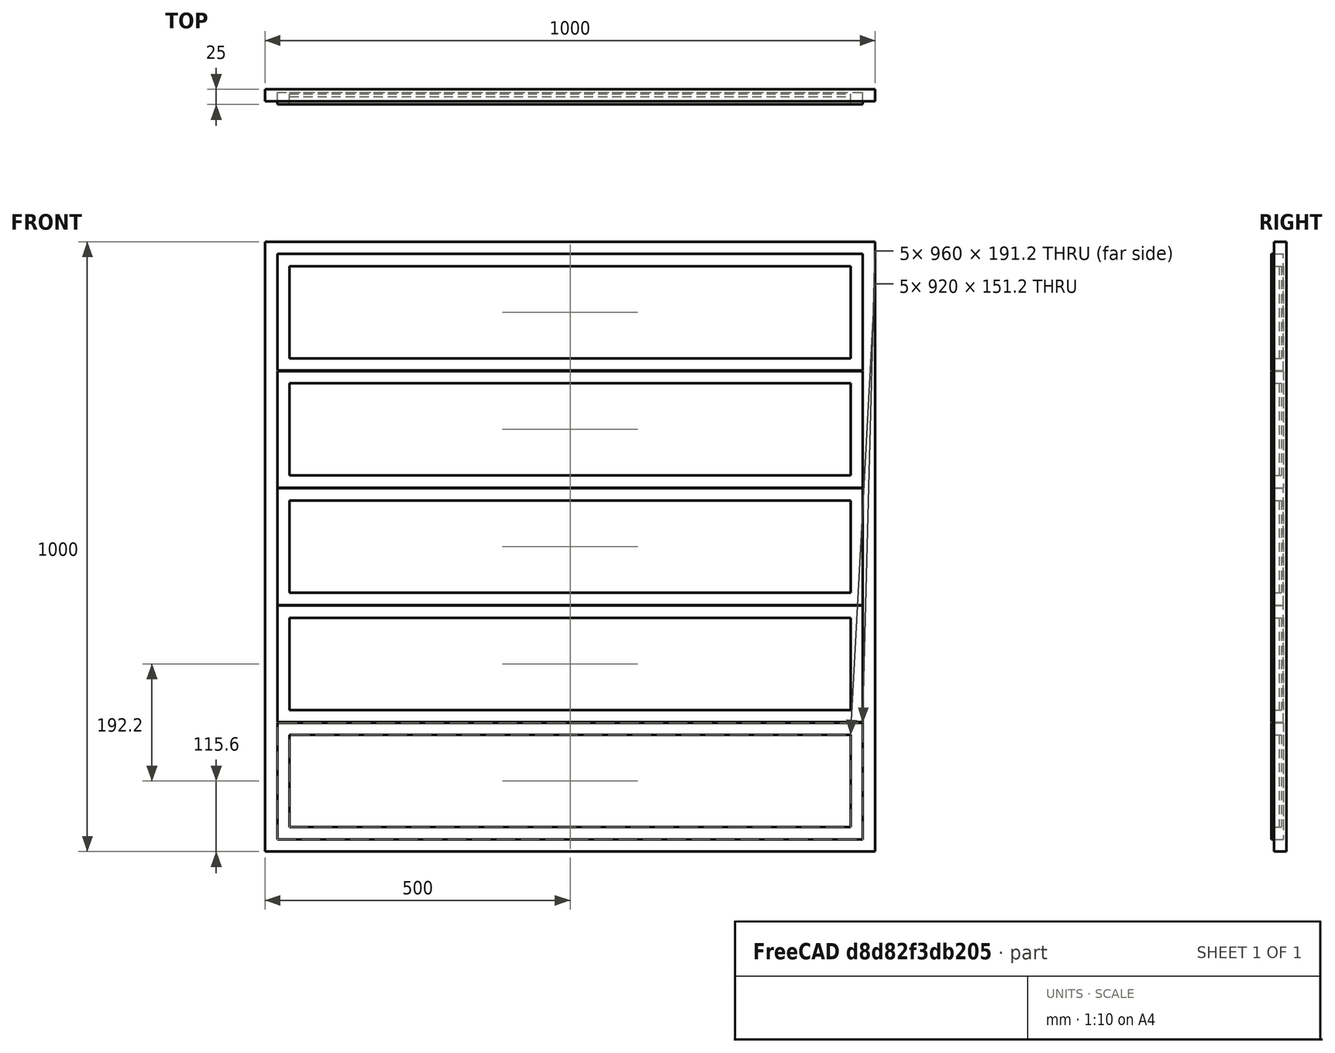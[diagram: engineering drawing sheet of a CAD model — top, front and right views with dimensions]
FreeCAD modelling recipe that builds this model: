
FCSTD DOCUMENT  (FreeCAD 0.16R6704 (Git))
Label: Tilting window 5 modules
License: CreativeCommons Attribution
LicenseURL: http://creativecommons.org/licenses/by/4.0/
objects: Sketcher::SketchObject×1, Part::FeaturePython×1
note: 2 computed .brp shape members not serialized (recipe doc carries the construction recipe); baked Part::Feature solids carry a one-line shape summary decoded from their .brp

FEATURE [Sketcher::SketchObject] Sketch107
  Placement = pos=(0,0,0) rot=(1,0,0;1.5708rad)
  sketch-geometry (54):
    g0: LineSegment StartX=0 StartY=1000 StartZ=0 EndX=1000 EndY=1000 EndZ=0
    g1: LineSegment StartX=1000 StartY=1000 StartZ=0 EndX=1000 EndY=0 EndZ=0
    g2: LineSegment StartX=1000 StartY=0 StartZ=0 EndX=0 EndY=0 EndZ=0
    g3: LineSegment StartX=0 StartY=0 StartZ=0 EndX=0 EndY=1000 EndZ=0
    g4: LineSegment StartX=20 StartY=980 StartZ=0 EndX=980 EndY=980 EndZ=0
    g5: LineSegment StartX=980 StartY=980 StartZ=0 EndX=980 EndY=788.8 EndZ=0
    g6: LineSegment StartX=980 StartY=20 StartZ=0 EndX=20 EndY=20 EndZ=0
    g7: LineSegment StartX=20 StartY=20 StartZ=0 EndX=20 EndY=211.2 EndZ=0
    g8: LineSegment StartX=40 StartY=960 StartZ=0 EndX=960 EndY=960 EndZ=0
    g9: LineSegment StartX=960 StartY=960 StartZ=0 EndX=960 EndY=808.8 EndZ=0
    g10: LineSegment StartX=960 StartY=808.8 StartZ=0 EndX=40 EndY=808.8 EndZ=0
    g11: LineSegment StartX=40 StartY=808.8 StartZ=0 EndX=40 EndY=960 EndZ=0
    g12: LineSegment StartX=20 StartY=788.8 StartZ=0 EndX=980 EndY=788.8 EndZ=0
    g13: LineSegment StartX=20 StartY=788.8 StartZ=0 EndX=20 EndY=980 EndZ=0
    g14: LineSegment StartX=980 StartY=787.8 StartZ=0 EndX=20 EndY=787.8 EndZ=0
    g15: LineSegment StartX=980 StartY=787.8 StartZ=0 EndX=980 EndY=596.6 EndZ=0
    g16: LineSegment StartX=20 StartY=596.6 StartZ=0 EndX=980 EndY=596.6 EndZ=0
    g17: LineSegment StartX=20 StartY=595.6 StartZ=0 EndX=980 EndY=595.6 EndZ=0
    g18: LineSegment StartX=20 StartY=596.6 StartZ=0 EndX=20 EndY=787.8 EndZ=0
    g19: LineSegment StartX=20 StartY=404.4 StartZ=0 EndX=980 EndY=404.4 EndZ=0
    g20: LineSegment StartX=20 StartY=403.4 StartZ=0 EndX=980 EndY=403.4 EndZ=0
    g21: LineSegment StartX=20 StartY=404.4 StartZ=0 EndX=20 EndY=595.6 EndZ=0
    g22: LineSegment StartX=20 StartY=212.2 StartZ=0 EndX=980 EndY=212.2 EndZ=0
    g23: LineSegment StartX=20 StartY=211.2 StartZ=0 EndX=980 EndY=211.2 EndZ=0
    g24: LineSegment StartX=20 StartY=212.2 StartZ=0 EndX=20 EndY=403.4 EndZ=0
    g25: LineSegment StartX=980 StartY=211.2 StartZ=0 EndX=980 EndY=20 EndZ=0
    g26: LineSegment StartX=980 StartY=403.4 StartZ=0 EndX=980 EndY=212.2 EndZ=0
    g27: LineSegment StartX=980 StartY=595.6 StartZ=0 EndX=980 EndY=404.4 EndZ=0
    g28: LineSegment StartX=40 StartY=767.8 StartZ=0 EndX=960 EndY=767.8 EndZ=0
    g29: LineSegment StartX=960 StartY=767.8 StartZ=0 EndX=960 EndY=616.6 EndZ=0
    g30: LineSegment StartX=960 StartY=616.6 StartZ=0 EndX=40 EndY=616.6 EndZ=0
    g31: LineSegment StartX=40 StartY=616.6 StartZ=0 EndX=40 EndY=767.8 EndZ=0
    g32: LineSegment StartX=40 StartY=575.6 StartZ=0 EndX=960 EndY=575.6 EndZ=0
    g33: LineSegment StartX=960 StartY=575.6 StartZ=0 EndX=960 EndY=424.4 EndZ=0
    g34: LineSegment StartX=960 StartY=424.4 StartZ=0 EndX=40 EndY=424.4 EndZ=0
    g35: LineSegment StartX=40 StartY=424.4 StartZ=0 EndX=40 EndY=575.6 EndZ=0
    g36: LineSegment StartX=40 StartY=383.4 StartZ=0 EndX=960 EndY=383.4 EndZ=0
    g37: LineSegment StartX=960 StartY=383.4 StartZ=0 EndX=960 EndY=232.2 EndZ=0
    g38: LineSegment StartX=960 StartY=232.2 StartZ=0 EndX=40 EndY=232.2 EndZ=0
    g39: LineSegment StartX=40 StartY=232.2 StartZ=0 EndX=40 EndY=383.4 EndZ=0
    g40: LineSegment StartX=40 StartY=191.2 StartZ=0 EndX=960 EndY=191.2 EndZ=0
    g41: LineSegment StartX=960 StartY=191.2 StartZ=0 EndX=960 EndY=40 EndZ=0
    g42: LineSegment StartX=960 StartY=40 StartZ=0 EndX=40 EndY=40 EndZ=0
    g43: LineSegment StartX=40 StartY=40 StartZ=0 EndX=40 EndY=191.2 EndZ=0
    g44: LineSegment [constr] StartX=905 StartY=616.6 StartZ=0 EndX=905 EndY=596.6 EndZ=0
    g45: LineSegment [constr] StartX=920.045 StartY=595.6 StartZ=0 EndX=920.045 EndY=575.6 EndZ=0
    g46: LineSegment [constr] StartX=918.223 StartY=232.2 StartZ=0 EndX=918.223 EndY=212.2 EndZ=0
    g47: LineSegment [constr] StartX=906.676 StartY=211.2 StartZ=0 EndX=906.676 EndY=191.2 EndZ=0
    g48: LineSegment [constr] StartX=919.529 StartY=40 StartZ=0 EndX=919.529 EndY=20 EndZ=0
    g49: LineSegment [constr] StartX=918 StartY=787.8 StartZ=0 EndX=918 EndY=767.8 EndZ=0
    g50: LineSegment [constr] StartX=882.731 StartY=424.4 StartZ=0 EndX=882.731 EndY=404.4 EndZ=0
    g51: LineSegment [constr] StartX=914 StartY=403.4 StartZ=0 EndX=914 EndY=383.4 EndZ=0
    g52: LineSegment [constr] StartX=936.524 StartY=980 StartZ=0 EndX=936.524 EndY=960 EndZ=0
    g53: LineSegment [constr] StartX=937.642 StartY=808.8 StartZ=0 EndX=937.642 EndY=788.8 EndZ=0
  constraints (153):
    c: Coincident(g0,g1)
    c: Coincident(g1,g2)
    c: Coincident(g2,g3)
    c: Coincident(g3,g0)
    c: Horizontal(g0)
    c: Horizontal(g2)
    c: Vertical(g1)
    c: Vertical(g3)
    c: DistanceX(g0,g0) = 1000  'Largura do vão'
    c: DistanceY(g1,g0) = 1000  'Altura do vão'
    c: Coincident(g2,g-1)
    c: Coincident(g4,g5)
    c: Coincident(g25,g6)
    c: Coincident(g6,g7)
    c: Coincident(g13,g4)
    c: Horizontal(g4)
    c: Horizontal(g6)
    c: Vertical(g5)
    c: Vertical(g7)
    c: DistanceX(g0,g4) = 20  'Largura perfil vertical 1'
    c: DistanceY(g4,g0) = 20  'Altura perfil superior'
    c: DistanceX(g4,g0) = 20  'Largura perfil vertical 2'
    c: DistanceY(g1,g25) = 20  'Altura perfil inferior'
    c: Coincident(g8,g9)
    c: Coincident(g9,g10)
    c: Coincident(g10,g11)
    c: Coincident(g11,g8)
    c: Horizontal(g8)
    c: Horizontal(g10)
    c: Vertical(g9)
    c: Vertical(g11)
    c: Coincident(g18,g14)
    c: Coincident(g13,g12)
    c: Tangent(g7,g13)
    c: Coincident(g5,g12)
    c: Coincident(g15,g14)
    c: Tangent(g5,g15)
    c: DistanceY(g18,g12) = 1
    c: Coincident(g21,g17)
    c: Coincident(g18,g16)
    c: Tangent(g7,g18)
    c: Coincident(g24,g20)
    c: Coincident(g21,g19)
    c: Tangent(g7,g21)
    c: Coincident(g7,g23)
    c: Coincident(g24,g22)
    c: Tangent(g7,g24)
    c: Coincident(g26,g22)
    c: Coincident(g25,g23)
    c: Tangent(g15,g25)
    c: Coincident(g27,g19)
    c: Coincident(g26,g20)
    c: Tangent(g15,g26)
    c: Coincident(g15,g16)
    c: Coincident(g27,g17)
    c: Tangent(g15,g27)
    c: DistanceY(g17,g16) = 1
    c: Horizontal(g16)
    c: Horizontal(g17)
    c: Horizontal(g19)
    c: Horizontal(g20)
    c: Horizontal(g22)
    c: Horizontal(g23)
    c: DistanceY(g20,g19) = 1
    c: DistanceY(g7,g22) = 1
    c: Horizontal(g12)
    c: Horizontal(g14)
    c: Equal(g5,g15)
    c: Equal(g15,g27)
    c: Equal(g27,g26)
    c: Equal(g26,g25)
    c: Coincident(g28,g29)
    c: Coincident(g29,g30)
    c: Coincident(g30,g31)
    c: Coincident(g31,g28)
    c: Horizontal(g28)
    c: Horizontal(g30)
    c: Vertical(g29)
    c: Vertical(g31)
    c: Coincident(g32,g33)
    c: Coincident(g33,g34)
    c: Coincident(g34,g35)
    c: Coincident(g35,g32)
    c: Horizontal(g32)
    c: Horizontal(g34)
    c: Vertical(g33)
    c: Vertical(g35)
    c: Coincident(g36,g37)
    c: Coincident(g37,g38)
    c: Coincident(g38,g39)
    c: Coincident(g39,g36)
    c: Horizontal(g36)
    c: Horizontal(g38)
    c: Vertical(g37)
    c: Vertical(g39)
    c: Coincident(g40,g41)
    c: Coincident(g41,g42)
    c: Coincident(g42,g43)
    c: Coincident(g43,g40)
    c: Horizontal(g40)
    c: Horizontal(g42)
    c: Vertical(g41)
    c: Vertical(g43)
    c: DistanceX(g10,g28) = 0
    c: DistanceX(g32,g30) = 0
    c: DistanceX(g36,g34) = 0
    c: DistanceX(g38,g40) = 0
    c: DistanceX(g37,g40) = 0
    c: DistanceX(g33,g36) = 0
    c: DistanceX(g29,g32) = 0
    c: DistanceX(g9,g28) = 0
    c: DistanceY(g8,g4) = 20  'Altura perfis horizonais janelas'
    c: DistanceX(g8,g4) = 20  'Largura perfil vertical 2 janelas'
    c: DistanceX(g4,g8) = 20  'Largura vertical 1 janelas'
    c: PointOnObject(g44,g30)  'Constraint117'
    c: PointOnObject(g44,g16)  'Constraint116'
    c: Vertical(g44)
    c: PointOnObject(g45,g17)
    c: PointOnObject(g45,g32)
    c: Vertical(g45)
    c: PointOnObject(g46,g38)
    c: PointOnObject(g46,g22)
    c: Vertical(g46)
    c: PointOnObject(g47,g23)
    c: PointOnObject(g47,g40)
    c: Vertical(g47)
    c: PointOnObject(g48,g42)
    c: PointOnObject(g48,g6)
    c: Vertical(g48)
    c: PointOnObject(g49,g14)
    c: PointOnObject(g49,g28)
    c: Vertical(g49)
    c: PointOnObject(g50,g34)
    c: PointOnObject(g50,g19)
    c: Vertical(g50)
    c: PointOnObject(g51,g20)
    c: PointOnObject(g51,g36)
    c: Vertical(g51)
    c: PointOnObject(g52,g4)
    c: PointOnObject(g52,g8)
    c: Vertical(g52)
    c: PointOnObject(g53,g10)
    c: PointOnObject(g53,g12)
    c: Vertical(g53)
    c: Equal(g52,g53)
    c: Equal(g53,g49)
    c: Equal(g49,g44)
    c: Equal(g44,g45)
    c: Equal(g45,g50)
    c: Equal(g50,g51)
    c: Equal(g51,g46)
    c: Equal(g46,g47)
    c: Equal(g47,g48)
FEATURE [Part::FeaturePython] Window079  label="Tilting window 5 modules"  # WARN: FeaturePython — macro-defined, semantics opaque (R4)
  Base = -> Sketch107
  Height = 0
  HoleDepth = 0
  MoveWithHost = true
  Normal = (0,1,0)
  Preset = 0
  Role = 0
  Width = 0
  WindowParts = MONTANTES | Frame | Wire0,Wire1,Wire2,Wire3,Wire4,Wire5,Wire6,Wire7 | 20.0 | 0.0 | MONTANTE 1 | Frame | Wire1,Wire3 | 20.0 | -5.0 | VIDRO 1 | Glass panel | Wire3 | 4.0 | 8.0 | MONTANTE 2 | Frame | Wire4,Wire7 | 20.0 | -5.0 | VIDRO 2 | Glass panel | Wire7 | 4.0 | 8.0 | MONTANTE 3 | Frame | Wire5,Wire8 | 20.0 | -5.0 | VIDRO 3 | Glass panel | Wire8 | 4.0 | 8.0 | VIDRO 4 | Glass panel | Wire9 | 4.0 | 8.0 | VIDRO 5 | Glass panel | Wire10 | 4.0 | 8.0 | MONTANTE 4 | Frame | Wire2,Wire10 | 20.0 | -5.0 | MONTANTE 5 | Frame | Wire9,Wire6 | 20.0 | -5.0
